# Revit family: IS_Linda-X_T4626_BIM_NL
name_source: partatom
category: Plumbing Fixtures
units: mm (PartAtom-declared; Revit-internal decimal feet)

## family parameters
Always vertical = No
Cut with Voids When Loaded = No
OmniClass Number = 23.45.05.14.21
OmniClass Title = Bathtubs
Part Type = Normal
Room Calculation Point = No
Round Connector Dimension = Use Diameter
Shared = No
Work Plane-Based = No

## types (1)
- T4626EN - LINDA FREESTANDING TUB  180X80 SOLID SURFACE - MATT WHITE
    Accessories = https://www.idealstandard.nl
    Afmetingen = 850 x 1738 x 494 mm
    AfstandsEenheid = Millimeter
    Afwerking = Mattweiß
    AreaUnits = Millimetres
    Artikelnummer = T4626EN
    Artikelomschrijving = 175cm x 85cm Freistehende Solid Surface Badewanne
    Artikelreferentie = LINDA FREESTANDING TUB  180X80 SOLID SURFACE
    AssetType = Fixed
    Auteur = Ideal Standard
    BIMObjectName = IS_IdealStandard_Baths_Linda-X_T4626
    BIMobject category = Bath & Spas
    BIMobject category code = sanitary-bath-spas
    BIMobject main category = Sanitary
    BIMobject main category code = sanitary
    BarCode = 8014140483533
    Barcode = 8014140483533
    BathType = Freestanding
    Beschrijvinggarantie = Herstellergarantie
    BimObjectNaam = IS_IdealStandard_Baths_Linda-X_T4626
    Brand = Ideal Standard
    Brand url = https://www.idealstandard.nl
    Breedte = 849.230268
    BrutoGewicht = 0
    Color = Weiß
    ConnectionType = Plumbing
    Cost = 0 $
    CurrencyUnit = €
    CurrentRevision = 1
    Date of publishing = 22/07/2021
    Description = 175cm x 85cm Freistehende Solid Surface Badewanne
    Diepte = 0 mm  [stored 0 ft]
    DrainSize = 0 mm  [stored 0 ft]
    DurationUnit = Years
    DuurEenheid = Jahre
    Edition number = 1
    Eigenschappen = 175cm x 85cm freistehende Badewanne Mineralwerkstoff-Badewanne mit Clicker-Ablauf und integriertem Schlitzüberlauf
    Features = 175cm x 85cm freestanding bath tub solid surface bath with clicker waste and integrated slotted overflow
    Finish = Matt White
    GTIN code = https://8014140483533
    Garantieunits = Jahre
    GemaaktOp = 21/07/2021
    HasGrabHandles = No
    Help = https://www.idealstandard.nl
    Hulp = https://www.idealstandard.nl
    IFC Classification = Sanitary Terminal
    IfcExportAs = IfcSanitaryTerminalType
    IfcExportType = BATH
    Installatieinstructies = https://www.idealstandard.nl
    Installation instructions = https://www.idealstandard.nl
    InstallationInstructions = https://www.idealstandard.nl
    Kleur = Weiß
    Lengte = 1738 mm
    LinearUnits = Millimitres
    MainColor = White
    MaintenanceInformation = https://www.idealstandard.nl
    Manufacturer = Ideal Standard
    Manufacturer name = Ideal Standard
    ManufacturerURL = https://www.idealstandard.nl
    Masterformat 2014 Code = 22 41 19
    Masterformat 2014 Description = Residential Bathtubs
    Materiaal = Solid Surface
    Material = Solid Surface
    Material main = Solid Surface
    MaterialThickness = 0 mm  [stored 0 ft]
    Merk = Ideal Standard
    Model = T4626EN
    ModelNumber = T4626EN
    ModelReference = LINDA FREESTANDING TUB  180X80 SOLID SURFACE
    Montageinstuctie = https://www.idealstandard.nl
    NBS Reference Code = 45-35-70/311
    NBS Reference Description = Baths
    Name = Baths_Linda-X_T4626_IdealStandard
    NettWeight = 184,00
    Nettogewicht = 0
    NominalDepth = 1738 mm
    NominalHeight = 494 mm
    NominalLength = 1738 mm
    NominalWidth = 849 mm
    OmniClass Code = 23-31 15 00
    OmniClass Description = Bathtubs
    OppervlakteEenheid = Millimeter
    OutletConnectionSize = 0 mm  [stored 0 ft]
    PredefinedType = Bath
    Product Guid = 6fa3239c-5c1b-4303-b97d-a8f194e09682
    Product SKU = T4626
    Product certification = https://www.idealstandard.nl
    Product data url = https://bimobject.com
    Product family = Sanitary
    Product group = Baths
    Product name = LINDA FREESTANDING TUB 180X80 SOLID SURFACE
    Product url = https://www.idealstandard.nl
    ProductInformation = https://www.idealstandard.nl
    ProductSoort = Ovale freistehende Badewanne
    Productinformatie = https://www.idealstandard.nl
    QR code = http://bimobject.com
    Revisie = 1
    Shape = Oval
    Size = 850 x 1738 x 494 mm
    Space = Internal
    SpareParts = https://www.idealstandard.nl
    SpilloverLevel = 0 mm  [stored 0 ft]
    Technical description = https://www.idealstandard.nl
    Telefoonnummer = 077 355 08 08
    Typeconnectie = Installation
    UNSPSC Code = 30181501
    URL = https://www.idealstandard.nl
    Uniclass 1.4 Code = L7211
    Uniclass 1.4 Description = Baths
    Uniclass 2.0 Code = PR-35-06-08
    Uniclass 2.0 Description = Baths
    Uniclass 2015 Code = Pr_40_20_06_08
    Uniclass 2015 Name = Baths
    Uniclass2015Beschrijving = Baths
    Uniclass2015Code = Pr_40_20_06_08
    Uniclass2015Referentie = Pr_40_20_06_08
    Uniclass2015Title = Baths
    Uniclass2015Version = v1.20
    Urlproducent = https://www.idealstandard.nl
    ValutaEenheid = Euro
    Versie = 1
    Version = 1
    Vervangingskosten = 0
    VolumeUnits = Litres
    Volumeunits = Liter
    Vorm = Oval
    WRASURL = https://www.wrasapprovals.co.uk
    WarrantyDescription = manufacturer warranty
    WarrantyDurationUnit = Years
    Wisselstukken = https://www.idealstandard.nl
    Youtube clip = https://www.youtube.com

note: [stored X ft] marks values corroborated as IEEE doubles in the binary element streams (Revit-internal decimal feet)

## geometry (parser evidence)
native form markers: Sweep x3
no freeform markers — native parametric forms only
